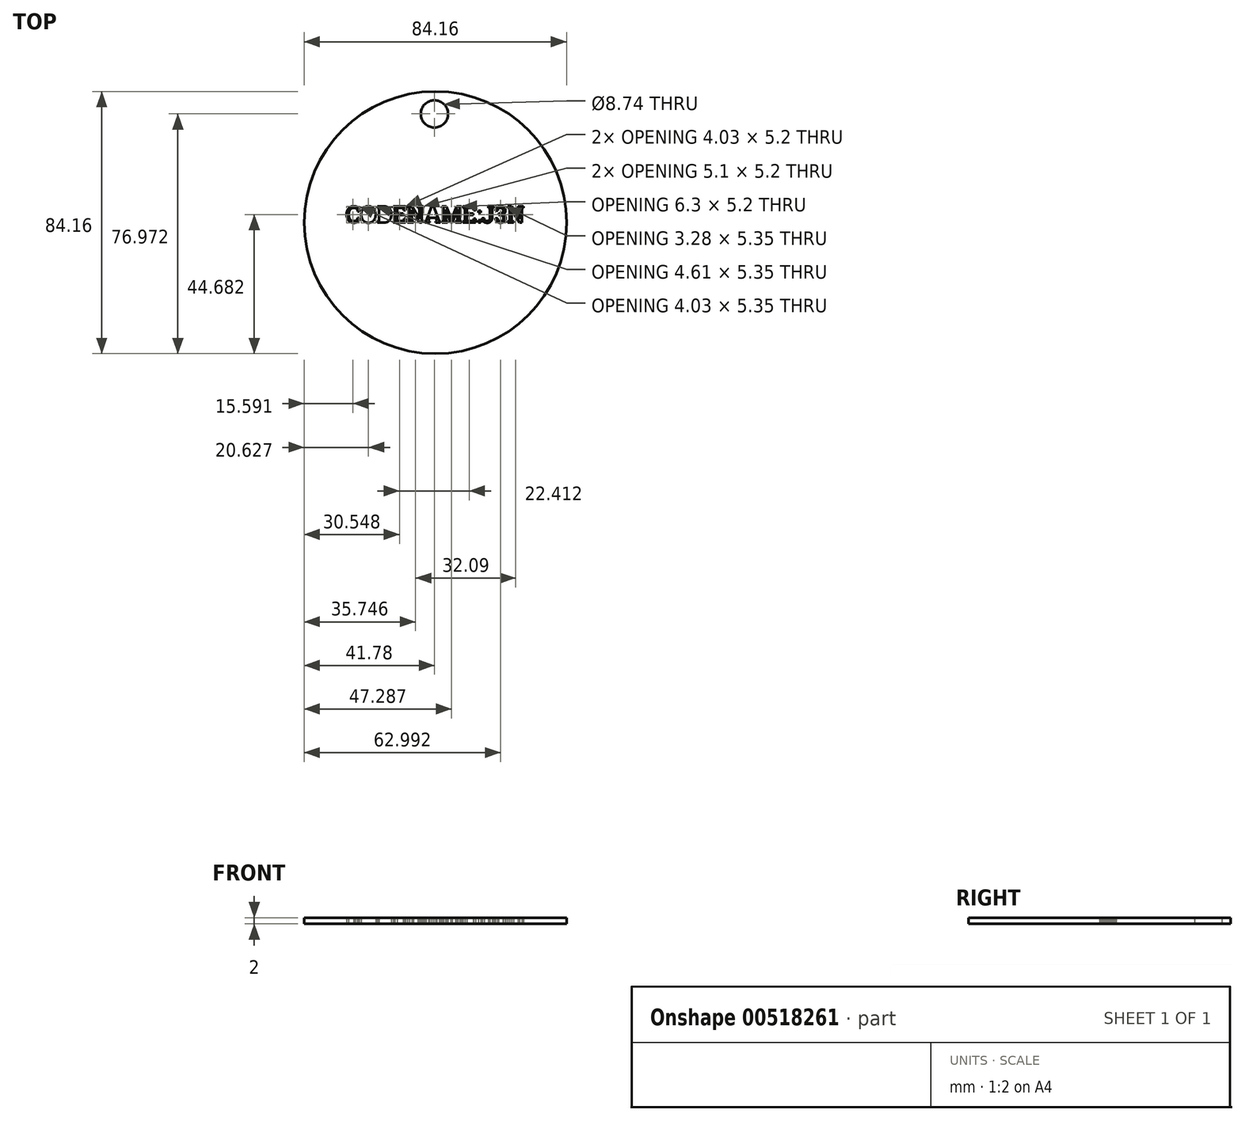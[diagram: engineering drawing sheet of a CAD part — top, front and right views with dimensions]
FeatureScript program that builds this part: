
annotation { "Feature Type Name" : "Feature", "Feature Type Description" : "" }
export const myFeature = defineFeature(function(context is Context, id is Id, definition is map)
    precondition{}
    {
        {
            var Q0;
            Q0=qCreatedBy(makeId("Top.planeOp"),FACE);
            var sketch = newSketch(context, id + "F0", { "sketchPlane" : qUnion([Q0])});
            skText(sketch, "E0", { "text": "CODENAME:J3N\n", "fontName": "RobotoSlab-Regular.ttf"});
            skCircle(sketch, "E1", {"center": v(0.3, 11.46) * mm, "radius": 42.08 * mm});
            skCircle(sketch, "E2", {"center": v(0, 46.35) * mm, "radius": 4.37 * mm});
            const initialGuessF0  = {"E0": [-0.02846, 0.01146, 1, 0, 0.00527]};
            skSetInitialGuess(sketch, initialGuessF0);
            skSolve(sketch);
        }
        {
            var Q0;
            Q0=makeQuery(id+"F0.imprint","IMPRINT",FACE,{"disambiguationData":[TD([[makeQuery(id+"F0.imprint","IMPRINT",EDGE,{"derivedFrom":sQuery(id+"F0.wireOp",EDGE,"E0.sketch_text.stroke-0")}),1.0]])]});
            extrude(context, id + "F1", {"entities" : qUnion([Q0]), "depth" : 2 * mm, "offsetDistance" : 25.4 * mm});
        }
    });
